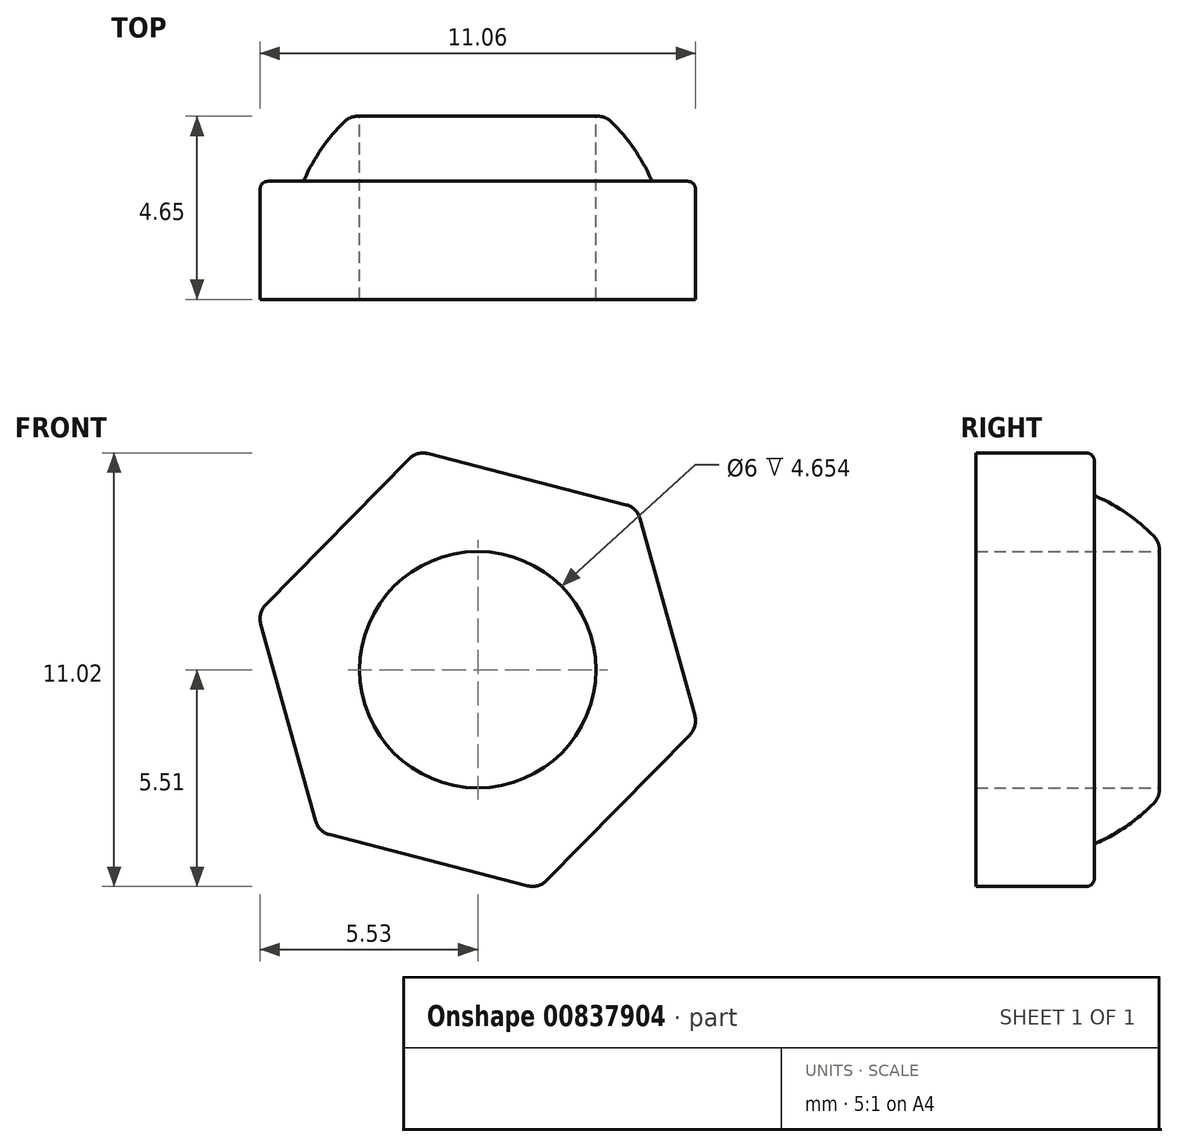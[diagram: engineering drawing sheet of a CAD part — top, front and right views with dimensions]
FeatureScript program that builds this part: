
annotation { "Feature Type Name" : "Feature", "Feature Type Description" : "" }
export const myFeature = defineFeature(function(context is Context, id is Id, definition is map)
    precondition{}
    {
        {
            var Q0;
            Q0=qCreatedBy(makeId("Front.planeOp"),FACE);
            var sketch = newSketch(context, id + "F0", { "sketchPlane" : qUnion([Q0])});
            skCircle(sketch, "E0.cCircle", {"center": v(0, 0) * mm, "radius": 5 * mm, "construction": true});
            skLineSegment(sketch, "E0.0", {"start": v(5.59, -1.45) * mm, "end": v(1.54, -5.56) * mm});
            skLineSegment(sketch, "E0.1", {"start": v(1.54, -5.56) * mm, "end": v(-4.05, -4.12) * mm});
            skLineSegment(sketch, "E0.2", {"start": v(-4.05, -4.12) * mm, "end": v(-5.59, 1.45) * mm});
            skLineSegment(sketch, "E0.3", {"start": v(-5.59, 1.45) * mm, "end": v(-1.54, 5.56) * mm});
            skLineSegment(sketch, "E0.4", {"start": v(-1.54, 5.56) * mm, "end": v(4.05, 4.12) * mm});
            skLineSegment(sketch, "E0.5", {"start": v(4.05, 4.12) * mm, "end": v(5.59, -1.45) * mm});
            skPoint(sketch, "E0.0.midPoint", {"position": v(3.57, -3.5) * mm});
            skSolve(sketch);
        }
        {
            var Q0;
            Q0=qSketchRegion(id+"F0",true);
            extrude(context, id + "F1", {"entities" : qUnion([Q0]), "depth" : 3 * mm, "offsetDistance" : 25 * mm});
        }
        {
            var Q0;
            Q0=qCreatedBy(makeId("Right.planeOp"),FACE);
            var sketch = newSketch(context, id + "F2", { "sketchPlane" : qUnion([Q0])});
            skLineSegment(sketch, "E1", {"start": v(193.74, 0) * mm, "end": v(-252.87, 0) * mm, "construction": true});
            skArc(sketch, "E2", {"start": v(1.65, 3.24) * mm, "mid": v(0.81, 3.98) * mm, "end": v(-0.17, 4.5) * mm});
            skLineSegment(sketch, "E3", {"start": v(1.65, 3.24) * mm, "end": v(1.65, 0) * mm});
            skLineSegment(sketch, "E4", {"start": v(-0.17, 4.5) * mm, "end": v(-0.17, 0) * mm});
            skLineSegment(sketch, "E5", {"start": v(5.98, 0) * mm, "end": v(-9.29, 0) * mm, "construction": true});
            skLineSegment(sketch, "E6", {"start": v(1.65, 0) * mm, "end": v(-0.17, 0) * mm});
            skPoint(sketch, "E7.trimOffspring.end.orphan", {"position": v(1.65, -3.24) * mm});
            skPoint(sketch, "E8.orphan", {"position": v(-0.17, -4.5) * mm});
            skSolve(sketch);
        }
        {
            var Q0;
            Q0=qSketchRegion(id+"F2",true);
            var Q1;
            Q1=sQuery(id+"F2.wireOp",EDGE,"E5");
            revolve(context, id + "F3", {"surfaceOperationType" : NewSurfaceOperationType.NEW, "entities" : qUnion([Q0]), "axis" : qUnion([Q1]), "revolveType" : RevolveType.FULL});
        }
        {
            var Q0;
            Q0=makeQuery(id+"F3.opRevolve","SWEPT_EDGE",EDGE,{"disambiguationData":[OSD([sQuery(id+"F2.wireOp",EDGE,"E2"),sQuery(id+"F2.wireOp",EDGE,"E3")])]});
            fillet(context, id + "F4", {"entities" : qUnion([Q0]), "radius" : 0.5 * mm, "tangentPropagation" : true, "allowEdgeOverflow" : false});
        }
        {
            var Q0;
            Q0=makeQuery(id+"F3.opRevolve","SWEPT_BODY",BODY,{"disambiguationData":[OSD([sQuery(id+"F2.wireOp",EDGE,"E2"),sQuery(id+"F2.wireOp",EDGE,"E3"),sQuery(id+"F2.wireOp",EDGE,"E4"),sQuery(id+"F2.wireOp",EDGE,"E6")])]});
            var Q1;
            Q1=makeQuery(id+"F1.opExtrude","SWEPT_BODY",BODY,{"disambiguationData":[OSD([sQuery(id+"F0.wireOp",EDGE,"E0.0"),sQuery(id+"F0.wireOp",EDGE,"E0.1"),sQuery(id+"F0.wireOp",EDGE,"E0.2"),sQuery(id+"F0.wireOp",EDGE,"E0.3"),sQuery(id+"F0.wireOp",EDGE,"E0.4"),sQuery(id+"F0.wireOp",EDGE,"E0.5")])]});
            booleanBodies(context, id + "F5", {"operationType" : BooleanOperationType.UNION, "tools" : qUnion([Q0, Q1])});
        }
        {
            var Q0;
            Q0=makeQuery(id+"F5.opBoolean","INTERSECT",EDGE,{"derivedFrom":[makeQuery(id+"F1.opExtrude","CAP_FACE",FACE,{"disambiguationData":[OSD([sQuery(id+"F0.wireOp",EDGE,"E0.0"),sQuery(id+"F0.wireOp",EDGE,"E0.1"),sQuery(id+"F0.wireOp",EDGE,"E0.2"),sQuery(id+"F0.wireOp",EDGE,"E0.3"),sQuery(id+"F0.wireOp",EDGE,"E0.4"),sQuery(id+"F0.wireOp",EDGE,"E0.5")])],"isStart":true}),makeQuery(id+"F3.opRevolve","SWEPT_FACE",FACE,{"disambiguationData":[OSD([sQuery(id+"F2.wireOp",EDGE,"E2")])]})]});
            fillet(context, id + "F6", {"entities" : qUnion([Q0]), "radius" : 0.1 * mm, "tangentPropagation" : true, "allowEdgeOverflow" : false});
        }
        {
            var Q0;
            Q0=makeQuery(id+"F3.opRevolve","SWEPT_FACE",FACE,{"disambiguationData":[OSD([sQuery(id+"F2.wireOp",EDGE,"E3")])]});
            var sketch = newSketch(context, id + "F7", { "sketchPlane" : qUnion([Q0])});
            skCircle(sketch, "E9", {"center": v(0, 0) * mm, "radius": 3 * mm});
            skSolve(sketch);
        }
        {
            var Q0;
            Q0=qSketchRegion(id+"F7",true);
            extrude(context, id + "F8", {"entities" : qUnion([Q0]), "operationType" : NewBodyOperationType.REMOVE, "oppositeDirection" : true, "depth" : 25 * mm, "offsetDistance" : 25 * mm});
        }
        {
            var Q0;
            Q0=makeQuery(id+"F1.opExtrude","SWEPT_EDGE",EDGE,{"disambiguationData":[OSD([sQuery(id+"F0.wireOp",EDGE,"E0.2"),sQuery(id+"F0.wireOp",EDGE,"E0.3")])]});
            var Q1;
            Q1=makeQuery(id+"F1.opExtrude","SWEPT_EDGE",EDGE,{"disambiguationData":[OSD([sQuery(id+"F0.wireOp",EDGE,"E0.1"),sQuery(id+"F0.wireOp",EDGE,"E0.2")])]});
            var Q2;
            Q2=makeQuery(id+"F1.opExtrude","SWEPT_EDGE",EDGE,{"disambiguationData":[OSD([sQuery(id+"F0.wireOp",EDGE,"E0.0"),sQuery(id+"F0.wireOp",EDGE,"E0.1")])]});
            var Q3;
            Q3=makeQuery(id+"F1.opExtrude","SWEPT_EDGE",EDGE,{"disambiguationData":[OSD([sQuery(id+"F0.wireOp",EDGE,"E0.3"),sQuery(id+"F0.wireOp",EDGE,"E0.4")])]});
            var Q4;
            Q4=makeQuery(id+"F1.opExtrude","SWEPT_EDGE",EDGE,{"disambiguationData":[OSD([sQuery(id+"F0.wireOp",EDGE,"E0.0"),sQuery(id+"F0.wireOp",EDGE,"E0.5")])]});
            var Q5;
            Q5=makeQuery(id+"F1.opExtrude","SWEPT_EDGE",EDGE,{"disambiguationData":[OSD([sQuery(id+"F0.wireOp",EDGE,"E0.4"),sQuery(id+"F0.wireOp",EDGE,"E0.5")])]});
            fillet(context, id + "F9", {"entities" : qUnion([Q0, Q1, Q2, Q3, Q4, Q5]), "radius" : 0.5 * mm, "tangentPropagation" : true, "allowEdgeOverflow" : false});
        }
        {
            var Q0;
            Q0=makeQuery(id+"F1.opExtrude","CAP_EDGE",EDGE,{"disambiguationData":[OSD([sQuery(id+"F0.wireOp",EDGE,"E0.4")])],"isStart":true});
            var Q1;
            Q1=makeQuery(id+"F1.opExtrude","CAP_EDGE",EDGE,{"disambiguationData":[OSD([sQuery(id+"F0.wireOp",EDGE,"E0.5")])],"isStart":true});
            var Q2;
            {var subQ0=sQuery(id+"F0.wireOp",EDGE,"E0.5");var subQ1=sQuery(id+"F0.wireOp",EDGE,"E0.0");Q2=makeQuery(id+"F9.opFillet","BLEND_EDGE",EDGE,{"blendedFrom":[makeQuery(id+"F1.opExtrude","SWEPT_EDGE",EDGE,{"disambiguationData":[OSD([subQ1,subQ0])]}),makeQuery(id+"F1.opExtrude","CAP_FACE",FACE,{"disambiguationData":[OSD([subQ1,sQuery(id+"F0.wireOp",EDGE,"E0.1"),sQuery(id+"F0.wireOp",EDGE,"E0.2"),sQuery(id+"F0.wireOp",EDGE,"E0.3"),sQuery(id+"F0.wireOp",EDGE,"E0.4"),subQ0])],"isStart":true})],"blendedInto":[makeQuery(id+"F1.opExtrude","CAP_FACE",FACE,{"disambiguationData":[OSD([subQ1,sQuery(id+"F0.wireOp",EDGE,"E0.1"),sQuery(id+"F0.wireOp",EDGE,"E0.2"),sQuery(id+"F0.wireOp",EDGE,"E0.3"),sQuery(id+"F0.wireOp",EDGE,"E0.4"),subQ0])],"isStart":true})]});}
            var Q3;
            {var subQ0=sQuery(id+"F0.wireOp",EDGE,"E0.5");var subQ1=sQuery(id+"F0.wireOp",EDGE,"E0.4");Q3=makeQuery(id+"F9.opFillet","BLEND_EDGE",EDGE,{"blendedFrom":[makeQuery(id+"F1.opExtrude","SWEPT_EDGE",EDGE,{"disambiguationData":[OSD([subQ1,subQ0])]}),makeQuery(id+"F1.opExtrude","CAP_FACE",FACE,{"disambiguationData":[OSD([sQuery(id+"F0.wireOp",EDGE,"E0.0"),sQuery(id+"F0.wireOp",EDGE,"E0.1"),sQuery(id+"F0.wireOp",EDGE,"E0.2"),sQuery(id+"F0.wireOp",EDGE,"E0.3"),subQ1,subQ0])],"isStart":true})],"blendedInto":[makeQuery(id+"F1.opExtrude","CAP_FACE",FACE,{"disambiguationData":[OSD([sQuery(id+"F0.wireOp",EDGE,"E0.0"),sQuery(id+"F0.wireOp",EDGE,"E0.1"),sQuery(id+"F0.wireOp",EDGE,"E0.2"),sQuery(id+"F0.wireOp",EDGE,"E0.3"),subQ1,subQ0])],"isStart":true})]});}
            var Q4;
            Q4=makeQuery(id+"F1.opExtrude","CAP_EDGE",EDGE,{"disambiguationData":[OSD([sQuery(id+"F0.wireOp",EDGE,"E0.0")])],"isStart":true});
            var Q5;
            {var subQ0=sQuery(id+"F0.wireOp",EDGE,"E0.1");var subQ1=sQuery(id+"F0.wireOp",EDGE,"E0.0");Q5=makeQuery(id+"F9.opFillet","BLEND_EDGE",EDGE,{"blendedFrom":[makeQuery(id+"F1.opExtrude","SWEPT_EDGE",EDGE,{"disambiguationData":[OSD([subQ1,subQ0])]}),makeQuery(id+"F1.opExtrude","CAP_FACE",FACE,{"disambiguationData":[OSD([subQ1,subQ0,sQuery(id+"F0.wireOp",EDGE,"E0.2"),sQuery(id+"F0.wireOp",EDGE,"E0.3"),sQuery(id+"F0.wireOp",EDGE,"E0.4"),sQuery(id+"F0.wireOp",EDGE,"E0.5")])],"isStart":true})],"blendedInto":[makeQuery(id+"F1.opExtrude","CAP_FACE",FACE,{"disambiguationData":[OSD([subQ1,subQ0,sQuery(id+"F0.wireOp",EDGE,"E0.2"),sQuery(id+"F0.wireOp",EDGE,"E0.3"),sQuery(id+"F0.wireOp",EDGE,"E0.4"),sQuery(id+"F0.wireOp",EDGE,"E0.5")])],"isStart":true})]});}
            var Q6;
            Q6=makeQuery(id+"F1.opExtrude","CAP_EDGE",EDGE,{"disambiguationData":[OSD([sQuery(id+"F0.wireOp",EDGE,"E0.1")])],"isStart":true});
            var Q7;
            {var subQ0=sQuery(id+"F0.wireOp",EDGE,"E0.2");var subQ1=sQuery(id+"F0.wireOp",EDGE,"E0.1");Q7=makeQuery(id+"F9.opFillet","BLEND_EDGE",EDGE,{"blendedFrom":[makeQuery(id+"F1.opExtrude","SWEPT_EDGE",EDGE,{"disambiguationData":[OSD([subQ1,subQ0])]}),makeQuery(id+"F1.opExtrude","CAP_FACE",FACE,{"disambiguationData":[OSD([sQuery(id+"F0.wireOp",EDGE,"E0.0"),subQ1,subQ0,sQuery(id+"F0.wireOp",EDGE,"E0.3"),sQuery(id+"F0.wireOp",EDGE,"E0.4"),sQuery(id+"F0.wireOp",EDGE,"E0.5")])],"isStart":true})],"blendedInto":[makeQuery(id+"F1.opExtrude","CAP_FACE",FACE,{"disambiguationData":[OSD([sQuery(id+"F0.wireOp",EDGE,"E0.0"),subQ1,subQ0,sQuery(id+"F0.wireOp",EDGE,"E0.3"),sQuery(id+"F0.wireOp",EDGE,"E0.4"),sQuery(id+"F0.wireOp",EDGE,"E0.5")])],"isStart":true})]});}
            var Q8;
            Q8=makeQuery(id+"F1.opExtrude","CAP_EDGE",EDGE,{"disambiguationData":[OSD([sQuery(id+"F0.wireOp",EDGE,"E0.2")])],"isStart":true});
            var Q9;
            {var subQ0=sQuery(id+"F0.wireOp",EDGE,"E0.3");var subQ1=sQuery(id+"F0.wireOp",EDGE,"E0.2");Q9=makeQuery(id+"F9.opFillet","BLEND_EDGE",EDGE,{"blendedFrom":[makeQuery(id+"F1.opExtrude","SWEPT_EDGE",EDGE,{"disambiguationData":[OSD([subQ1,subQ0])]}),makeQuery(id+"F1.opExtrude","CAP_FACE",FACE,{"disambiguationData":[OSD([sQuery(id+"F0.wireOp",EDGE,"E0.0"),sQuery(id+"F0.wireOp",EDGE,"E0.1"),subQ1,subQ0,sQuery(id+"F0.wireOp",EDGE,"E0.4"),sQuery(id+"F0.wireOp",EDGE,"E0.5")])],"isStart":true})],"blendedInto":[makeQuery(id+"F1.opExtrude","CAP_FACE",FACE,{"disambiguationData":[OSD([sQuery(id+"F0.wireOp",EDGE,"E0.0"),sQuery(id+"F0.wireOp",EDGE,"E0.1"),subQ1,subQ0,sQuery(id+"F0.wireOp",EDGE,"E0.4"),sQuery(id+"F0.wireOp",EDGE,"E0.5")])],"isStart":true})]});}
            var Q10;
            Q10=makeQuery(id+"F1.opExtrude","CAP_EDGE",EDGE,{"disambiguationData":[OSD([sQuery(id+"F0.wireOp",EDGE,"E0.3")])],"isStart":true});
            var Q11;
            {var subQ0=sQuery(id+"F0.wireOp",EDGE,"E0.4");var subQ1=sQuery(id+"F0.wireOp",EDGE,"E0.3");Q11=makeQuery(id+"F9.opFillet","BLEND_EDGE",EDGE,{"blendedFrom":[makeQuery(id+"F1.opExtrude","SWEPT_EDGE",EDGE,{"disambiguationData":[OSD([subQ1,subQ0])]}),makeQuery(id+"F1.opExtrude","CAP_FACE",FACE,{"disambiguationData":[OSD([sQuery(id+"F0.wireOp",EDGE,"E0.0"),sQuery(id+"F0.wireOp",EDGE,"E0.1"),sQuery(id+"F0.wireOp",EDGE,"E0.2"),subQ1,subQ0,sQuery(id+"F0.wireOp",EDGE,"E0.5")])],"isStart":true})],"blendedInto":[makeQuery(id+"F1.opExtrude","CAP_FACE",FACE,{"disambiguationData":[OSD([sQuery(id+"F0.wireOp",EDGE,"E0.0"),sQuery(id+"F0.wireOp",EDGE,"E0.1"),sQuery(id+"F0.wireOp",EDGE,"E0.2"),subQ1,subQ0,sQuery(id+"F0.wireOp",EDGE,"E0.5")])],"isStart":true})]});}
            fillet(context, id + "F10", {"entities" : qUnion([Q0, Q1, Q2, Q3, Q4, Q5, Q6, Q7, Q8, Q9, Q10, Q11]), "radius" : 0.2 * mm, "tangentPropagation" : true, "allowEdgeOverflow" : false});
        }
    });
